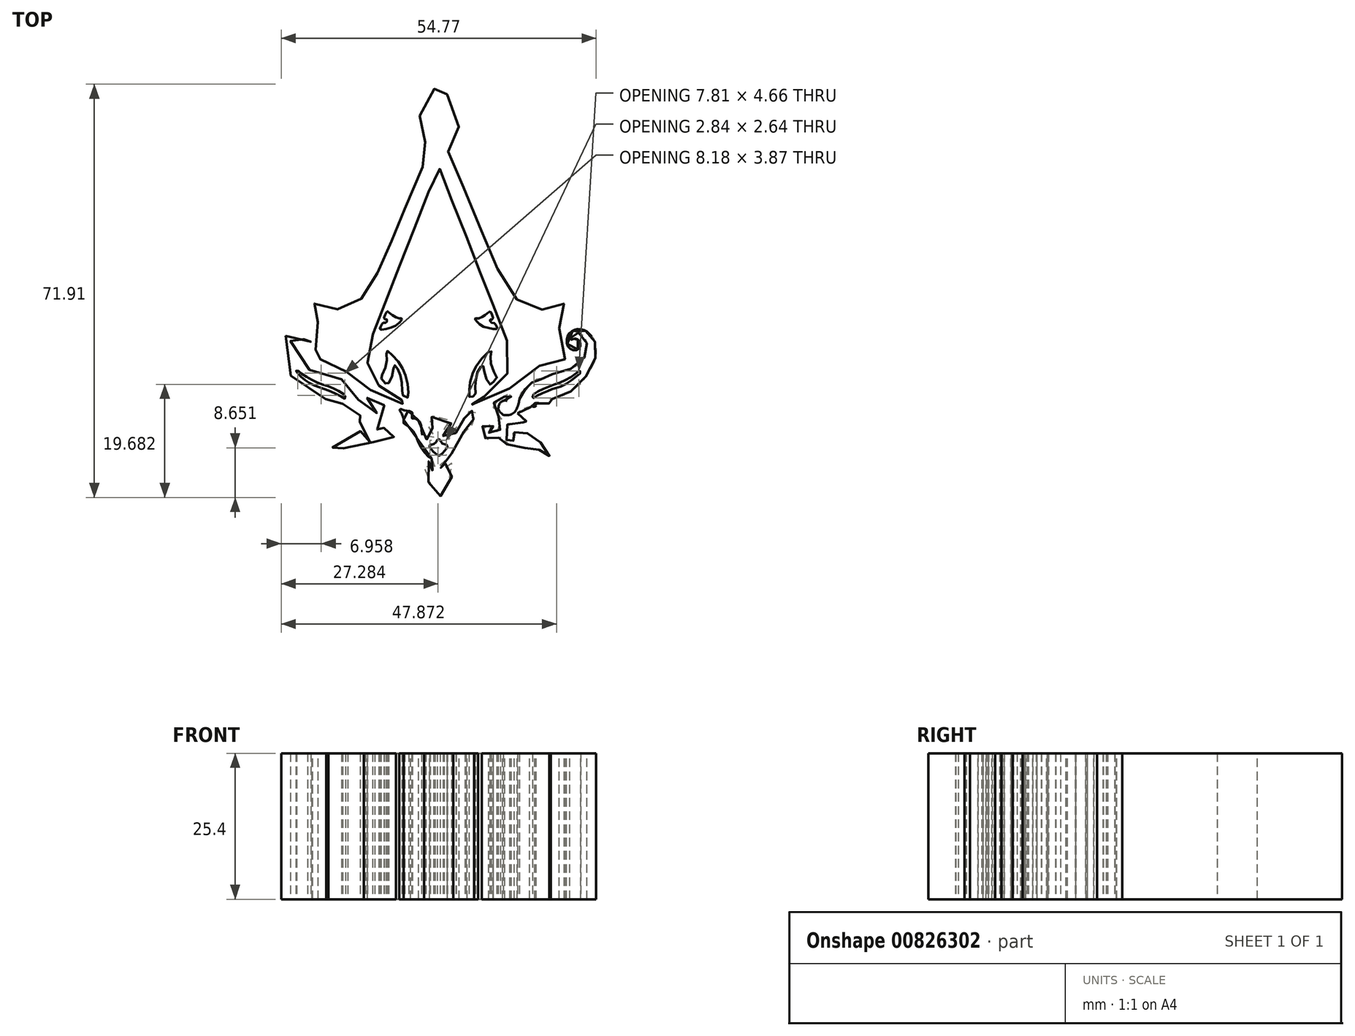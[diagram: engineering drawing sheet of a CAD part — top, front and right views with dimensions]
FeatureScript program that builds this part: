
annotation { "Feature Type Name" : "Feature", "Feature Type Description" : "" }
export const myFeature = defineFeature(function(context is Context, id is Id, definition is map)
    precondition{}
    {
        {
            var Q0;
            Q0=qCreatedBy(makeId("Top.planeOp"),FACE);
            var sketch = newSketch(context, id + "F0", { "sketchPlane" : qUnion([Q0])});
            skFitSpline(sketch, "E0", {"points": [v(-5.4, 0.86) * mm, v(-3.92, 4.33) * mm, v(-2.45, 7.77) * mm, v(-1.23, 10.58) * mm, v(-1.1, 10.98) * mm, v(-1.14, 11.26) * mm, v(-1.68, 12.2) * mm, v(-2.47, 13.46) * mm, v(-2.98, 14.9) * mm, v(-2.91, 16.18) * mm, v(-2.62, 17.6) * mm, v(-1.8, 19.52) * mm, v(-0.81, 21.06) * mm, v(-0.11, 21.91) * mm, v(0.36, 22.42) * mm, v(0.45, 22.51) * mm, v(0.55, 22.54) * mm, v(0.6, 22.53) * mm, v(0.73, 22.38) * mm, v(1.46, 21.53) * mm, v(2.83, 19.37) * mm, v(3.79, 17.06) * mm, v(4.04, 15.37) * mm, v(3.42, 13.46) * mm, v(2.27, 11.43) * mm, v(2.07, 11.07) * mm, v(2.1, 10.97) * mm, v(2.25, 10.64) * mm, v(3.3, 8.18) * mm, v(4.59, 5.15) * mm, v(6.1, 1.47) * mm, v(7.66, -2.26) * mm, v(9.11, -5.7) * mm, v(10.14, -8.16) * mm, v(11.34, -10.88) * mm, v(12.7, -13.16) * mm, v(14, -14.75) * mm, v(14.9, -15.5) * mm, v(16.12, -16.24) * mm, v(17.57, -16.6) * mm, v(19, -16.64) * mm, v(20.36, -16.34) * mm, v(21.65, -15.88) * mm, v(22.13, -15.67) * mm, v(22.25, -15.64) * mm, v(22.3, -15.65) * mm, v(22.39, -15.78) * mm, v(22.26, -16.04) * mm, v(21.81, -17.41) * mm, v(21.52, -19.25) * mm, v(21.48, -20.94) * mm, v(21.75, -23.24) * mm, v(22.39, -25.14) * mm, v(22.47, -25.33) * mm, v(22.27, -25.4) * mm, v(21.76, -25.24) * mm, v(20.5, -25.31) * mm, v(17.97, -26.49) * mm, v(16.02, -27.91) * mm, v(13.89, -29.66) * mm, v(11.72, -30.97) * mm, v(8.59, -32.42) * mm, v(6.1, -33.23) * mm, v(5.54, -33.3) * mm, v(5.5, -33.19) * mm, v(5.66, -33.09) * mm, v(6.16, -32.9) * mm, v(8.28, -31.91) * mm, v(10.33, -30.5) * mm, v(11.6, -29.24) * mm, v(12.47, -27.7) * mm, v(12.9, -25.62) * mm, v(12.72, -23.12) * mm, v(12.28, -21.75) * mm, v(11.42, -19.55) * mm, v(10.16, -16.38) * mm, v(9.52, -14.71) * mm, v(8.63, -12.53) * mm, v(7.68, -10.14) * mm], "startDerivative": vector(73.29, 168.51) * mm, "endDerivative": vector(-53.95, 139.34) * mm});
            skFitSpline(sketch, "E1", {"points": [v(7.68, -10.14) * mm, v(6.37, -6.77) * mm, v(5.38, -4.15) * mm, v(4.55, -1.97) * mm, v(3.04, 1.8) * mm, v(1.77, 4.96) * mm, v(0.78, 7.61) * mm, v(0.68, 7.8) * mm, v(0.47, 7.82) * mm, v(0.37, 7.63) * mm, v(-0.19, 6.31) * mm, v(-1.36, 3.45) * mm, v(-2.31, 0.92) * mm, v(-3.74, -2.58) * mm, v(-4.79, -5.36) * mm, v(-6.56, -9.72) * mm, v(-7.75, -12.97) * mm, v(-8.8, -15.6) * mm, v(-9.75, -17.88) * mm, v(-10.67, -20.38) * mm, v(-11.51, -22.54) * mm, v(-11.82, -24.07) * mm, v(-11.83, -26.07) * mm, v(-11.47, -27.38) * mm, v(-11.02, -28.44) * mm, v(-9.92, -29.85) * mm, v(-8.81, -30.82) * mm, v(-7.46, -31.76) * mm, v(-5.68, -32.55) * mm, v(-4.54, -33.07) * mm, v(-4.43, -33.1) * mm, v(-4.4, -33.26) * mm, v(-4.53, -33.31) * mm, v(-4.93, -33.26) * mm, v(-6.94, -32.67) * mm, v(-8.95, -31.92) * mm, v(-11.95, -30.29) * mm, v(-13.58, -29.13) * mm, v(-14.93, -27.98) * mm, v(-16.7, -26.67) * mm, v(-18.54, -25.68) * mm, v(-19.9, -25.34) * mm, v(-21, -25.4) * mm, v(-21.33, -25.45) * mm, v(-21.49, -25.26) * mm, v(-21.37, -24.97) * mm, v(-20.87, -23.67) * mm, v(-20.48, -21.72) * mm, v(-20.42, -19.97) * mm, v(-20.54, -18.48) * mm, v(-21.02, -16.78) * mm, v(-21.38, -15.91) * mm, v(-21.4, -15.76) * mm, v(-21.23, -15.63) * mm, v(-20.94, -15.75) * mm, v(-20, -16.14) * mm, v(-18.54, -16.55) * mm, v(-16.93, -16.63) * mm, v(-15.32, -16.33) * mm, v(-13.88, -15.57) * mm, v(-12.81, -14.65) * mm, v(-11.55, -12.98) * mm, v(-10.56, -11.26) * mm, v(-9.64, -9.22) * mm, v(-8.5, -6.63) * mm, v(-7.42, -4.09) * mm, v(-6.52, -1.9) * mm, v(-5.4, 0.86) * mm], "startDerivative": vector(-60.4, 153.82) * mm, "endDerivative": vector(55.5, 141.36) * mm});
            skFitSpline(sketch, "E2", {"points": [v(-9.32, -19.14) * mm, v(-9.64, -19.76) * mm, v(-9.72, -19.9) * mm, v(-9.64, -20.09) * mm, v(-9, -20.09) * mm, v(-7.48, -19.7) * mm, v(-6.4, -19.02) * mm, v(-5.88, -18.39) * mm, v(-5.89, -18.23) * mm, v(-6.06, -18.22) * mm, v(-6.6, -18.13) * mm, v(-7.38, -17.74) * mm, v(-8.12, -17.2) * mm, v(-8.34, -16.98) * mm, v(-8.46, -16.98) * mm, v(-8.55, -17.08) * mm, v(-8.8, -17.65) * mm, v(-9, -18.13) * mm, v(-8.93, -18.25) * mm, v(-8.66, -18.39) * mm, v(-8.5, -18.4) * mm, v(-8.44, -18.59) * mm, v(-8.58, -18.86) * mm, v(-8.75, -18.97) * mm, v(-9, -19) * mm, v(-9.25, -18.98) * mm, v(-9.32, -19.14) * mm]});
            skFitSpline(sketch, "E3", {"points": [v(8.97, -17.3) * mm, v(9.25, -17.08) * mm, v(9.44, -17) * mm, v(9.6, -17.08) * mm, v(9.75, -17.42) * mm, v(9.96, -18.1) * mm, v(9.94, -18.32) * mm, v(9.78, -18.43) * mm, v(9.6, -18.43) * mm, v(9.46, -18.41) * mm, v(9.4, -18.5) * mm, v(9.49, -18.74) * mm, v(9.72, -18.98) * mm, v(10.1, -19) * mm, v(10.25, -19.02) * mm, v(10.45, -19.29) * mm, v(10.69, -19.86) * mm, v(10.67, -20) * mm, v(10.45, -20.08) * mm, v(9.54, -19.95) * mm, v(8.36, -19.66) * mm, v(7.44, -19.07) * mm, v(6.9, -18.48) * mm, v(6.81, -18.23) * mm, v(6.9, -18.2) * mm, v(7.05, -18.2) * mm, v(7.52, -18.17) * mm, v(8.13, -17.9) * mm, v(8.66, -17.6) * mm, v(8.97, -17.3) * mm]});
            skFitSpline(sketch, "E4", {"points": [v(-7.34, -26.95) * mm, v(-7.58, -28.1) * mm, v(-7.85, -28.93) * mm, v(-8.36, -29.65) * mm, v(-8.58, -29.74) * mm, v(-8.8, -29.51) * mm, v(-9.27, -28.95) * mm, v(-9.53, -28.56) * mm, v(-9.54, -28.4) * mm, v(-9.4, -28.17) * mm, v(-8.91, -27.21) * mm, v(-8.62, -26.32) * mm, v(-8.5, -25.34) * mm, v(-8.52, -24.53) * mm, v(-8.64, -24.13) * mm, v(-8.6, -23.89) * mm, v(-8.4, -23.88) * mm, v(-8.05, -24.13) * mm, v(-7.15, -25.06) * mm, v(-6.44, -25.84) * mm, v(-5.8, -26.87) * mm, v(-5.4, -27.8) * mm, v(-5.02, -28.92) * mm, v(-4.8, -30.38) * mm, v(-4.73, -31.33) * mm, v(-4.76, -31.88) * mm, v(-4.89, -31.97) * mm, v(-5.2, -31.87) * mm, v(-5.77, -31.55) * mm, v(-5.87, -31.33) * mm, v(-5.85, -30.63) * mm, v(-5.88, -29.53) * mm, v(-6.03, -28.67) * mm, v(-6.3, -27.65) * mm, v(-6.58, -27.03) * mm, v(-6.92, -26.46) * mm, v(-7.06, -26.38) * mm, v(-7.24, -26.43) * mm, v(-7.3, -26.58) * mm, v(-7.34, -26.95) * mm]});
            skFitSpline(sketch, "E5", {"points": [v(6.98, -28.83) * mm, v(7.13, -27.93) * mm, v(7.53, -27.05) * mm, v(7.88, -26.57) * mm, v(8.07, -26.4) * mm, v(8.17, -26.4) * mm, v(8.28, -26.5) * mm, v(8.33, -26.88) * mm, v(8.44, -27.55) * mm, v(8.75, -28.63) * mm, v(9.18, -29.31) * mm, v(9.48, -29.72) * mm, v(9.73, -29.63) * mm, v(9.99, -29.3) * mm, v(10.47, -28.8) * mm, v(10.61, -28.55) * mm, v(10.42, -28.1) * mm, v(9.9, -27.01) * mm, v(9.58, -25.99) * mm, v(9.5, -25.14) * mm, v(9.57, -24.46) * mm, v(9.66, -24.08) * mm, v(9.65, -23.82) * mm, v(9.53, -23.82) * mm, v(9.08, -24.08) * mm, v(8, -25.2) * mm, v(7.01, -26.5) * mm, v(6.57, -27.45) * mm, v(6.14, -28.66) * mm, v(5.89, -29.91) * mm, v(5.81, -30.8) * mm, v(5.82, -31.74) * mm, v(5.88, -31.94) * mm, v(6.07, -31.95) * mm, v(6.55, -31.79) * mm, v(6.85, -31.63) * mm, v(6.9, -31.3) * mm, v(6.9, -30.63) * mm, v(6.9, -29.77) * mm, v(6.98, -28.83) * mm]});
            skFitSpline(sketch, "E6", {"points": [v(-22.98, -21.85) * mm, v(-22.63, -22.01) * mm, v(-22.44, -22.06) * mm, v(-22.32, -21.85) * mm, v(-22.37, -21.44) * mm, v(-22.8, -20.91) * mm, v(-23.36, -20.67) * mm, v(-24.12, -20.8) * mm, v(-25.03, -21.52) * mm, v(-25.26, -22.4) * mm, v(-25.25, -23.48) * mm, v(-25.1, -24.41) * mm, v(-24.68, -25.23) * mm, v(-24, -26.03) * mm, v(-23.06, -26.66) * mm, v(-21.98, -27.14) * mm, v(-20.6, -27.5) * mm, v(-18.68, -28.13) * mm, v(-17.6, -28.66) * mm, v(-17.45, -28.76) * mm, v(-17.34, -28.74) * mm, v(-17.2, -28.53) * mm, v(-17.1, -28.47) * mm, v(-16.92, -28.52) * mm, v(-16.32, -28.87) * mm, v(-15.56, -29.52) * mm, v(-14.95, -30.25) * mm, v(-14.76, -30.5) * mm, v(-14.66, -30.54) * mm, v(-14.6, -30.4) * mm, v(-14.45, -30.36) * mm, v(-14.3, -30.47) * mm, v(-13.92, -31.04) * mm, v(-13.5, -32) * mm, v(-13.42, -32.69) * mm, v(-13.4, -33.16) * mm, v(-13.26, -33.51) * mm, v(-12.94, -34.08) * mm, v(-12.45, -34.68) * mm, v(-11.98, -34.9) * mm, v(-11.42, -34.98) * mm, v(-10.68, -34.92) * mm, v(-10.24, -34.65) * mm, v(-10, -34.33) * mm, v(-9.91, -33.91) * mm, v(-9.93, -33.47) * mm, v(-10.15, -33) * mm, v(-10.58, -32.66) * mm, v(-10.99, -32.59) * mm, v(-11.4, -32.71) * mm, v(-11.58, -32.71) * mm, v(-11.74, -32.51) * mm, v(-11.88, -32.16) * mm, v(-12.1, -31.58) * mm, v(-12.17, -31.31) * mm, v(-12.08, -31.24) * mm, v(-11.74, -31.36) * mm, v(-10.98, -31.74) * mm, v(-9.8, -32.2) * mm, v(-9.42, -32.3) * mm, v(-9.13, -32.57) * mm, v(-8.98, -33.05) * mm, v(-9, -33.73) * mm, v(-9.27, -34.42) * mm, v(-10.01, -35.34) * mm, v(-10.34, -35.57) * mm, v(-10.54, -35.95) * mm, v(-10.6, -36.2) * mm, v(-10.6, -36.54) * mm, v(-10.55, -36.76) * mm, v(-10.35, -37.18) * mm, v(-10.02, -37.7) * mm, v(-9.7, -38.02) * mm, v(-9.33, -38.2) * mm, v(-8.95, -38.3) * mm, v(-8.7, -38.3) * mm, v(-8.35, -38.25) * mm, v(-8.17, -38.1) * mm, v(-8.24, -37.84) * mm, v(-8.43, -37.8) * mm, v(-8.76, -37.8) * mm, v(-8.9, -37.6) * mm, v(-9, -37.29) * mm, v(-8.89, -36.88) * mm, v(-8.62, -36.6) * mm, v(-8.15, -36.52) * mm, v(-7.6, -36.63) * mm, v(-7.16, -36.9) * mm, v(-6.95, -37.16) * mm, v(-6.9, -37.46) * mm, v(-6.93, -37.98) * mm, v(-7.1, -38.57) * mm, v(-7.55, -39.06) * mm, v(-8.08, -39.3) * mm, v(-8.55, -39.31) * mm, v(-9.25, -39.25) * mm, v(-9.6, -39.12) * mm, v(-9.97, -38.95) * mm, v(-10.12, -38.9) * mm, v(-10.25, -39) * mm, v(-10.35, -39.13) * mm, v(-10.54, -39.42) * mm, v(-10.78, -39.67) * mm, v(-11.3, -40) * mm, v(-11.87, -40.26) * mm, v(-12.33, -40.37) * mm, v(-13.04, -40.55) * mm, v(-14.1, -40.69) * mm, v(-14.83, -40.77) * mm, v(-15.44, -40.74) * mm, v(-16.06, -40.83) * mm, v(-16.9, -41.12) * mm, v(-17.46, -41.38) * mm, v(-18.01, -41.7) * mm, v(-18.28, -41.91) * mm, v(-18.5, -42.12) * mm, v(-18.65, -42.12) * mm, v(-18.68, -41.94) * mm, v(-18.56, -41.62) * mm, v(-18.23, -41.07) * mm, v(-17.8, -40.46) * mm, v(-17.32, -39.93) * mm, v(-16.65, -39.31) * mm, v(-15.74, -38.63) * mm, v(-15.04, -38.22) * mm, v(-14.24, -37.9) * mm, v(-13.67, -37.77) * mm, v(-13, -37.85) * mm, v(-12.36, -38.15) * mm, v(-12.04, -38.48) * mm, v(-11.9, -38.77) * mm, v(-11.96, -39.08) * mm, v(-12.25, -39.38) * mm, v(-12.45, -39.48) * mm, v(-12.5, -39.59) * mm, v(-12.5, -39.72) * mm, v(-12.32, -39.85) * mm, v(-11.95, -39.85) * mm, v(-11.59, -39.73) * mm, v(-11.27, -39.38) * mm, v(-11.05, -38.9) * mm, v(-10.99, -38.4) * mm, v(-11.03, -37.45) * mm, v(-11.25, -36.9) * mm, v(-11.61, -36.46) * mm, v(-12.18, -36.22) * mm, v(-12.92, -36.17) * mm, v(-13.83, -36.25) * mm, v(-14.57, -36.49) * mm, v(-15.06, -36.63) * mm, v(-15.23, -36.64) * mm, v(-15.29, -36.49) * mm, v(-15, -36.27) * mm, v(-14.4, -35.87) * mm, v(-13.68, -35.46) * mm, v(-13.24, -35.2) * mm, v(-13.15, -35.01) * mm, v(-13.23, -34.7) * mm, v(-13.46, -34.45) * mm, v(-13.92, -34.16) * mm, v(-14.58, -33.87) * mm, v(-15.35, -33.62) * mm, v(-15.92, -33.6) * mm, v(-16.27, -33.54) * mm, v(-16.37, -33.42) * mm, v(-16.23, -33.24) * mm, v(-16.18, -33.04) * mm, v(-16.32, -32.93) * mm, v(-16.77, -32.95) * mm, v(-17.46, -33.03) * mm, v(-18.29, -33.03) * mm, v(-18.81, -32.96) * mm, v(-19.03, -32.78) * mm, v(-18.9, -32.69) * mm, v(-18.63, -32.64) * mm, v(-18.62, -32.5) * mm, v(-18.87, -32.31) * mm, v(-19.35, -32.23) * mm, v(-19.94, -32.1) * mm, v(-20.87, -31.74) * mm, v(-22.53, -30.82) * mm, v(-23.78, -29.75) * mm, v(-24.76, -28.74) * mm, v(-25.6, -27.5) * mm, v(-26.33, -26.17) * mm, v(-26.73, -24.95) * mm, v(-26.87, -23.41) * mm, v(-26.71, -22.53) * mm, v(-26.18, -21.4) * mm, v(-25.59, -20.78) * mm, v(-24.85, -20.36) * mm, v(-24.12, -20.11) * mm, v(-23.28, -20.17) * mm, v(-22.7, -20.45) * mm, v(-22.06, -21.09) * mm, v(-21.73, -22.14) * mm, v(-22.07, -23.17) * mm, v(-22.81, -23.73) * mm, v(-23.62, -23.58) * mm, v(-24.08, -23.05) * mm, v(-24.13, -22.44) * mm, v(-23.76, -21.94) * mm, v(-23.34, -21.77) * mm, v(-22.98, -21.85) * mm]});
            skFitSpline(sketch, "E7", {"points": [v(-24.01, -27.76) * mm, v(-24.27, -27.48) * mm, v(-24.25, -27.23) * mm, v(-23.97, -27.27) * mm, v(-23.52, -27.7) * mm, v(-22.6, -28.3) * mm, v(-21.46, -28.91) * mm, v(-20.05, -29.57) * mm, v(-18.92, -29.94) * mm, v(-17.88, -30.32) * mm, v(-16.81, -30.86) * mm, v(-15.96, -31.43) * mm, v(-15.73, -31.72) * mm, v(-15.69, -32.03) * mm, v(-15.77, -32.14) * mm, v(-16.14, -31.98) * mm, v(-17.14, -31.41) * mm, v(-18.4, -30.86) * mm, v(-19.67, -30.39) * mm, v(-20.65, -30.07) * mm, v(-21.73, -29.57) * mm, v(-22.66, -28.98) * mm, v(-23.37, -28.42) * mm, v(-24.01, -27.76) * mm]});
            skFitSpline(sketch, "E8", {"points": [v(11.27, -34.59) * mm, v(10.98, -34.23) * mm, v(10.89, -33.83) * mm, v(10.99, -33.33) * mm, v(11.2, -32.9) * mm, v(11.45, -32.7) * mm, v(11.76, -32.55) * mm], "startDerivative": vector(-1.89, 1.96) * mm, "endDerivative": vector(2.4, 0.45) * mm});
            skFitSpline(sketch, "E9", {"points": [v(14.54, -32.24) * mm, v(14.67, -31.6) * mm, v(15.03, -31) * mm, v(15.4, -30.54) * mm, v(15.52, -30.5) * mm, v(15.65, -30.59) * mm, v(15.71, -30.67) * mm, v(15.88, -30.47) * mm, v(16.19, -29.97) * mm, v(16.67, -29.46) * mm, v(17.27, -28.95) * mm, v(17.85, -28.6) * mm, v(18.02, -28.55) * mm, v(18.16, -28.64) * mm, v(18.32, -28.8) * mm, v(18.62, -28.7) * mm, v(19.08, -28.41) * mm, v(19.46, -28.23) * mm, v(20.53, -27.84) * mm, v(22.06, -27.4) * mm, v(23.25, -27.07) * mm, v(24.36, -26.52) * mm, v(25.34, -25.74) * mm, v(25.89, -24.91) * mm, v(26.13, -24.23) * mm, v(26.22, -23.72) * mm, v(26.28, -22.65) * mm, v(26.1, -21.71) * mm, v(25.65, -21.17) * mm, v(25.1, -20.78) * mm, v(24.48, -20.61) * mm, v(23.93, -20.81) * mm, v(23.48, -21.29) * mm, v(23.33, -21.57) * mm, v(23.36, -21.83) * mm, v(23.43, -21.97) * mm, v(23.61, -21.95) * mm, v(23.98, -21.76) * mm, v(24.4, -21.75) * mm, v(24.85, -22) * mm, v(25.1, -22.33) * mm, v(25.18, -22.83) * mm, v(25, -23.35) * mm, v(24.5, -23.7) * mm, v(23.77, -23.71) * mm, v(23.17, -23.27) * mm, v(22.85, -22.71) * mm, v(22.78, -21.77) * mm, v(23.07, -21.03) * mm, v(23.7, -20.44) * mm, v(24.34, -20.13) * mm, v(25.07, -20.08) * mm, v(25.66, -20.2) * mm, v(26.33, -20.55) * mm, v(26.87, -21.06) * mm, v(27.4, -21.73) * mm, v(27.72, -22.38) * mm, v(27.86, -23.17) * mm, v(27.87, -24.57) * mm, v(27.7, -25.44) * mm, v(27.16, -26.67) * mm, v(26.1, -28.32) * mm, v(25, -29.7) * mm, v(23.75, -30.7) * mm, v(22.11, -31.64) * mm, v(20.79, -32.1) * mm, v(19.9, -32.29) * mm, v(19.74, -32.4) * mm, v(19.82, -32.55) * mm, v(20, -32.72) * mm, v(20, -32.9) * mm, v(19.75, -33) * mm, v(19.12, -32.95) * mm, v(18.11, -32.93) * mm, v(17.34, -32.91) * mm, v(17.23, -32.99) * mm, v(17.27, -33.17) * mm, v(17.42, -33.3) * mm, v(17.45, -33.4) * mm, v(17.35, -33.53) * mm, v(17.03, -33.57) * mm, v(16.21, -33.65) * mm, v(15.19, -34.01) * mm, v(14.53, -34.46) * mm, v(14.24, -34.72) * mm], "startDerivative": vector(6.22, 52.78) * mm, "endDerivative": vector(-26.89, -25.49) * mm});
            skFitSpline(sketch, "E10", {"points": [v(14.24, -34.72) * mm, v(14.16, -34.87) * mm, v(14.24, -35.16) * mm, v(14.77, -35.49) * mm, v(15.4, -35.87) * mm, v(15.95, -36.25) * mm, v(16.3, -36.54) * mm, v(16.3, -36.67) * mm, v(16.17, -36.71) * mm, v(15.78, -36.57) * mm, v(14.95, -36.25) * mm, v(14.18, -36.17) * mm, v(13.33, -36.2) * mm, v(12.53, -36.6) * mm, v(12.1, -37.38) * mm, v(12.02, -38.38) * mm, v(12.1, -38.94) * mm, v(12.47, -39.53) * mm, v(12.86, -39.82) * mm, v(13.31, -39.85) * mm, v(13.58, -39.78) * mm, v(13.65, -39.62) * mm, v(13.46, -39.47) * mm, v(13.23, -39.3) * mm, v(13.03, -39) * mm, v(13.03, -38.68) * mm, v(13.26, -38.36) * mm, v(13.7, -38.03) * mm, v(14.24, -37.84) * mm, v(14.85, -37.8) * mm, v(15.34, -37.9) * mm, v(15.95, -38.18) * mm, v(16.48, -38.48) * mm, v(17.16, -38.92) * mm, v(17.86, -39.46) * mm, v(18.55, -40.16) * mm, v(19.2, -40.97) * mm, v(19.7, -41.81) * mm, v(19.77, -42.13) * mm, v(19.65, -42.18) * mm, v(19.55, -42.16) * mm, v(19.28, -41.91) * mm, v(18.64, -41.41) * mm, v(17.99, -41.06) * mm, v(17.42, -40.86) * mm, v(16.84, -40.78) * mm, v(16.11, -40.76) * mm, v(15.4, -40.76) * mm, v(14.39, -40.62) * mm, v(13.18, -40.37) * mm, v(12.35, -40.1) * mm, v(11.76, -39.52) * mm, v(11.44, -39.12) * mm, v(11.35, -38.93) * mm, v(11.22, -38.9) * mm, v(11, -38.96) * mm, v(10.55, -39.2) * mm, v(9.87, -39.32) * mm, v(9.19, -39.28) * mm, v(8.69, -39.08) * mm, v(8.34, -38.78) * mm, v(8.18, -38.36) * mm, v(8, -37.74) * mm, v(8.08, -37.1) * mm, v(8.35, -36.75) * mm, v(8.92, -36.56) * mm, v(9.4, -36.53) * mm, v(9.8, -36.66) * mm, v(10.02, -37.07) * mm, v(9.96, -37.56) * mm, v(9.74, -37.81) * mm, v(9.4, -37.89) * mm, v(9.25, -37.86) * mm, v(9.23, -37.93) * mm, v(9.23, -38.06) * mm, v(9.43, -38.26) * mm, v(9.8, -38.35) * mm, v(10.34, -38.3) * mm, v(10.86, -37.94) * mm, v(11.42, -37.24) * mm, v(11.65, -36.33) * mm, v(11.47, -35.78) * mm, v(11.01, -35.34) * mm, v(10.5, -34.86) * mm, v(10.12, -34.09) * mm, v(10, -33.36) * mm, v(10.18, -32.68) * mm, v(10.38, -32.35) * mm, v(10.55, -32.26) * mm, v(10.78, -32.24) * mm, v(11.4, -32.02) * mm, v(12.28, -31.65) * mm, v(12.71, -31.4) * mm, v(12.94, -31.22) * mm, v(13.04, -31.22) * mm, v(13.16, -31.44) * mm, v(13.1, -31.85) * mm, v(12.86, -32.4) * mm, v(12.68, -32.63) * mm, v(12.39, -32.55) * mm, v(12.05, -32.46) * mm, v(11.76, -32.55) * mm], "startDerivative": vector(-17.74, -23.7) * mm, "endDerivative": vector(-36.9, -16.36) * mm});
            skFitSpline(sketch, "E11", {"points": [v(11.27, -34.59) * mm, v(11.55, -34.88) * mm, v(11.84, -35) * mm, v(12.66, -35.01) * mm, v(13.16, -34.88) * mm, v(13.63, -34.59) * mm, v(14, -34.1) * mm, v(14.24, -33.56) * mm, v(14.45, -32.94) * mm, v(14.5, -32.55) * mm, v(14.54, -32.24) * mm], "startDerivative": vector(3.26, -3.6) * mm, "endDerivative": vector(0.62, 3.88) * mm});
            skFitSpline(sketch, "E12", {"points": [v(19.53, -30.82) * mm, v(18.08, -31.46) * mm, v(17.16, -31.95) * mm, v(17, -32.09) * mm, v(16.9, -32.08) * mm, v(16.84, -31.74) * mm, v(17.08, -31.35) * mm, v(18.11, -30.7) * mm, v(19.46, -30.14) * mm, v(20.84, -29.63) * mm, v(22.11, -29.13) * mm, v(23.56, -28.38) * mm, v(24.34, -27.83) * mm, v(24.8, -27.43) * mm, v(25.01, -27.33) * mm, v(25.17, -27.47) * mm, v(25.16, -27.7) * mm, v(24.6, -28.21) * mm, v(23.16, -29.3) * mm, v(21.85, -30) * mm, v(20.78, -30.35) * mm, v(20.14, -30.54) * mm, v(19.53, -30.82) * mm]});
            skFitSpline(sketch, "E13", {"points": [v(-0.67, -42.59) * mm, v(-0.28, -42.75) * mm, v(-0.01, -42.81) * mm, v(0.11, -42.84) * mm, v(0.2, -43.43) * mm, v(0.22, -44.02) * mm, v(0.05, -44.3) * mm, v(-0.27, -44.58) * mm, v(-0.59, -44.68) * mm, v(-0.83, -44.6) * mm, v(-0.93, -44.38) * mm, v(-0.83, -44.18) * mm, v(-0.64, -44.17) * mm, v(-0.44, -44.09) * mm, v(-0.38, -43.77) * mm, v(-0.5, -43.42) * mm, v(-0.77, -43.2) * mm, v(-1.17, -43.09) * mm, v(-1.64, -43.23) * mm, v(-1.94, -43.66) * mm, v(-2.04, -44.36) * mm, v(-2.02, -45.03) * mm, v(-1.7, -45.92) * mm, v(-1.16, -46.84) * mm, v(-0.6, -47.55) * mm, v(-0.1, -48.24) * mm, v(0.25, -48.87) * mm, v(0.34, -49.21) * mm, v(0.53, -49.36) * mm, v(0.71, -49.31) * mm, v(0.81, -49.06) * mm, v(0.88, -48.81) * mm, v(1.07, -48.32) * mm, v(1.48, -47.74) * mm, v(1.98, -47.02) * mm, v(2.42, -46.4) * mm, v(2.73, -45.9) * mm, v(3.04, -44.83) * mm, v(3, -44.13) * mm, v(2.87, -43.6) * mm, v(2.62, -43.23) * mm, v(2.21, -43.13) * mm, v(1.83, -43.23) * mm, v(1.56, -43.47) * mm, v(1.49, -43.73) * mm, v(1.57, -44.05) * mm, v(1.66, -44.2) * mm, v(1.86, -44.31) * mm, v(1.89, -44.42) * mm, v(1.83, -44.59) * mm, v(1.63, -44.65) * mm, v(1.17, -44.55) * mm, v(0.93, -44.27) * mm, v(0.8, -44) * mm, v(0.77, -43.55) * mm, v(0.77, -43.18) * mm, v(0.92, -42.86) * mm, v(1.02, -42.8) * mm, v(1.73, -42.65) * mm, v(2.45, -42.12) * mm, v(3.1, -41.31) * mm, v(3.69, -40.53) * mm, v(4.01, -39.65) * mm, v(4.37, -38.8) * mm, v(4.65, -38.18) * mm, v(4.99, -37.77) * mm, v(5.37, -37.36) * mm, v(5.9, -36.9) * mm, v(6.28, -36.65) * mm, v(6.4, -36.63) * mm, v(6.63, -36.52) * mm, v(6.69, -36.31) * mm, v(6.62, -36.15) * mm, v(6.54, -35.87) * mm, v(6.55, -35.56) * mm, v(6.78, -34.95) * mm, v(7, -34.59) * mm, v(7.27, -34.29) * mm, v(7.34, -34.04) * mm, v(7.29, -33.94) * mm, v(7.01, -34.03) * mm, v(6.46, -34.23) * mm, v(5.91, -34.35) * mm, v(5.35, -34.41) * mm, v(5.12, -34.48) * mm, v(5.06, -34.59) * mm, v(5.08, -34.8) * mm, v(5.17, -34.98) * mm, v(5.24, -35.24) * mm, v(5.26, -35.43) * mm, v(5.17, -35.54) * mm, v(4.91, -35.62) * mm, v(4.56, -35.68) * mm, v(4.26, -35.87) * mm, v(3.92, -36.13) * mm, v(3.62, -36.58) * mm, v(3.51, -37.04) * mm, v(3.54, -37.54) * mm, v(3.5, -38) * mm, v(3.32, -38.65) * mm, v(3, -39.06) * mm, v(2.6, -39.26) * mm, v(2.11, -39.36) * mm, v(1.68, -39.34) * mm, v(1.43, -39.15) * mm, v(1.31, -38.89) * mm, v(1.32, -38.4) * mm, v(1.43, -37.74) * mm, v(1.56, -37.38) * mm, v(1.86, -37.12) * mm, v(2.19, -37) * mm, v(2.5, -37) * mm, v(2.66, -36.98) * mm, v(2.74, -36.77) * mm, v(2.53, -36.14) * mm, v(2.2, -35.64) * mm, v(1.75, -35.32) * mm, v(1.1, -35.09) * mm, v(0.1, -35.07) * mm, v(-0.46, -35.23) * mm, v(-1.03, -35.6) * mm, v(-1.4, -36.06) * mm, v(-1.63, -36.52) * mm, v(-1.68, -36.82) * mm, v(-1.61, -36.96) * mm, v(-1.34, -36.95) * mm, v(-1, -36.97) * mm, v(-0.6, -37.27) * mm, v(-0.33, -37.64) * mm, v(-0.19, -38.18) * mm, v(-0.15, -38.57) * mm, v(-0.22, -38.98) * mm, v(-0.56, -39.27) * mm, v(-0.9, -39.36) * mm, v(-1.36, -39.35) * mm, v(-1.78, -39.16) * mm, v(-2.15, -38.83) * mm, v(-2.43, -38.33) * mm, v(-2.46, -37.66) * mm, v(-2.5, -36.91) * mm, v(-2.68, -36.32) * mm, v(-3.32, -35.77) * mm, v(-3.76, -35.63) * mm, v(-4.13, -35.58) * mm, v(-4.19, -35.41) * mm, v(-4.12, -35.13) * mm, v(-4.03, -34.8) * mm, v(-4.1, -34.59) * mm, v(-4.24, -34.43) * mm, v(-4.86, -34.3) * mm, v(-5.57, -34.2) * mm, v(-6.08, -34) * mm, v(-6.28, -33.97) * mm, v(-6.34, -34.06) * mm, v(-6.2, -34.33) * mm, v(-5.86, -34.8) * mm, v(-5.58, -35.7) * mm, v(-5.58, -36.33) * mm, v(-5.6, -36.5) * mm, v(-5.41, -36.61) * mm, v(-5.08, -36.71) * mm, v(-4.67, -37.07) * mm, v(-3.86, -37.92) * mm, v(-3.36, -38.93) * mm, v(-2.89, -40) * mm, v(-2.45, -40.85) * mm, v(-1.63, -41.94) * mm, v(-1.06, -42.42) * mm, v(-0.67, -42.59) * mm]});
            skFitSpline(sketch, "E14", {"points": [v(-0.68, -40.14) * mm, v(-0.28, -40.03) * mm, v(0.1, -39.65) * mm, v(0.3, -39.3) * mm, v(0.4, -39.2) * mm, v(0.57, -39.2) * mm, v(0.66, -39.33) * mm, v(0.91, -39.69) * mm, v(1.28, -40.03) * mm, v(1.76, -40.16) * mm, v(2, -40.25) * mm, v(2.06, -40.42) * mm, v(1.82, -40.93) * mm, v(1.44, -41.4) * mm, v(0.99, -41.83) * mm, v(0.6, -42.09) * mm, v(0.55, -42.09) * mm, v(0.45, -42.04) * mm, v(0.02, -41.79) * mm, v(-0.4, -41.39) * mm, v(-0.74, -41.03) * mm, v(-1.04, -40.62) * mm, v(-1.08, -40.34) * mm, v(-0.96, -40.2) * mm, v(-0.86, -40.14) * mm, v(-0.68, -40.14) * mm]});
            skSolve(sketch);
        }
        {
            var Q0;
            Q0 = qSketchRegion(id + "F0", true);
            extrude(context, id + "F1", {"entities" : qUnion([Q0]), "depth" : 25.4 * mm, "offsetDistance" : 25.4 * mm});
        }
    });
